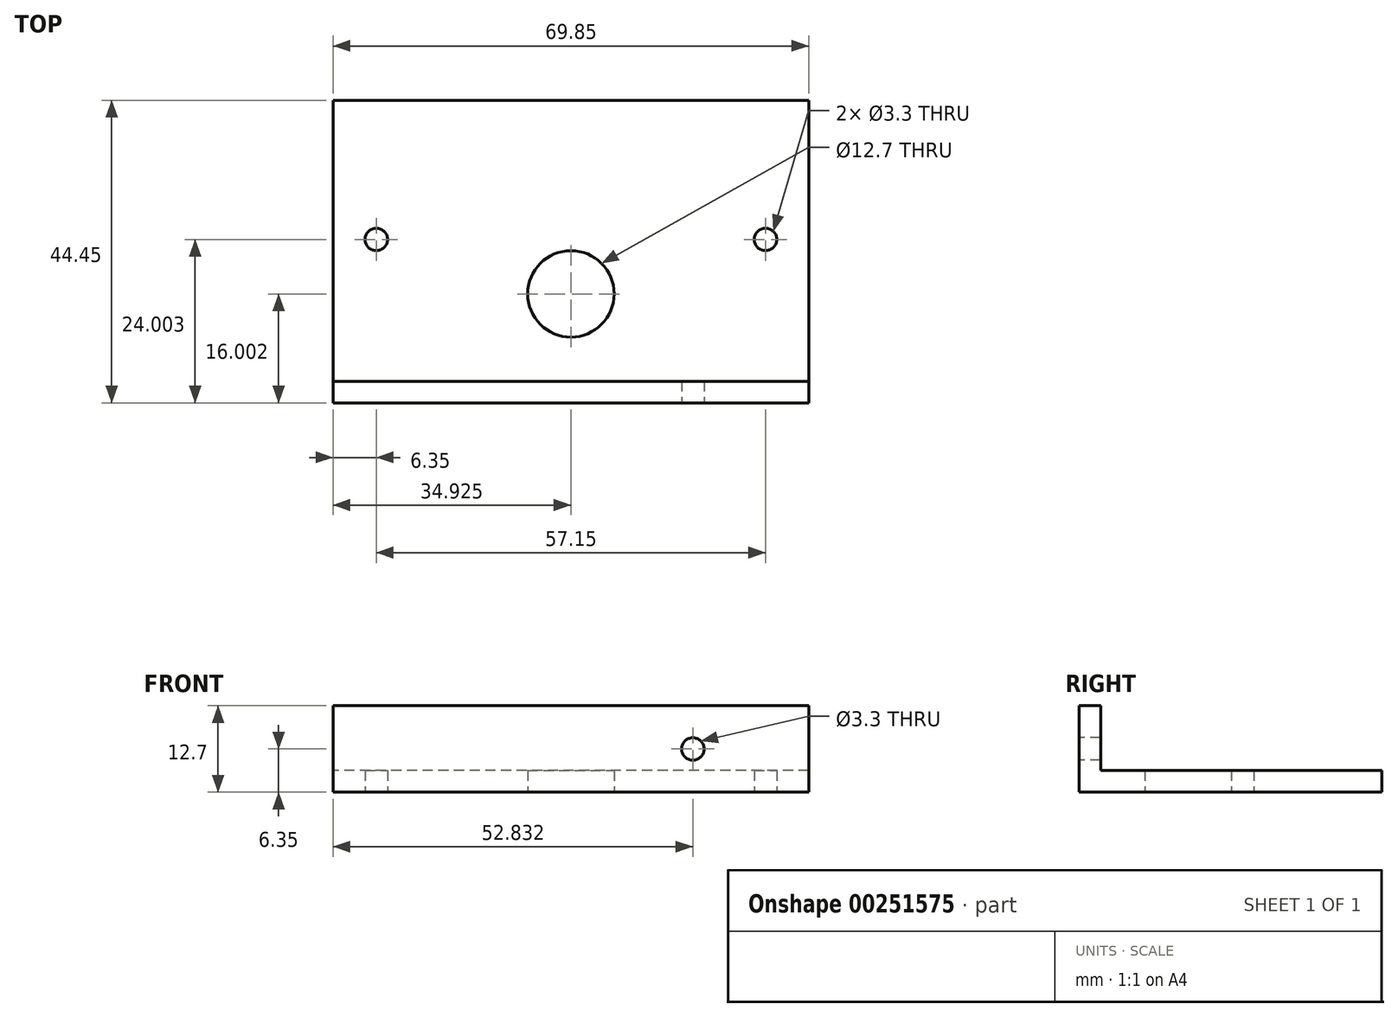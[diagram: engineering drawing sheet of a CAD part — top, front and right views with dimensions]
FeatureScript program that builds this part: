
annotation { "Feature Type Name" : "Feature", "Feature Type Description" : "" }
export const myFeature = defineFeature(function(context is Context, id is Id, definition is map)
    precondition{}
    {
        {
            var Q0;
            Q0=qCreatedBy(makeId("Right.planeOp"),FACE);
            var sketch = newSketch(context, id + "F0", { "sketchPlane" : qUnion([Q0])});
            skLineSegment(sketch, "E0", {"start": v(0, 0) * mm, "end": v(44.45, 0) * mm});
            skLineSegment(sketch, "E1", {"start": v(44.45, 0) * mm, "end": v(44.45, 3.18) * mm});
            skLineSegment(sketch, "E2", {"start": v(44.45, 3.18) * mm, "end": v(3.17, 3.18) * mm});
            skLineSegment(sketch, "E3", {"start": v(3.17, 3.18) * mm, "end": v(3.17, 12.7) * mm});
            skLineSegment(sketch, "E4", {"start": v(3.17, 12.7) * mm, "end": v(0, 12.7) * mm});
            skLineSegment(sketch, "E5", {"start": v(0, 12.7) * mm, "end": v(0, 0) * mm});
            skSolve(sketch);
        }
        {
            var Q0;
            Q0=qSketchRegion(id+"F0",true);
            extrude(context, id + "F1", {"entities" : qUnion([Q0]), "depth" : 69.85 * mm});
        }
        {
            var Q0;
            Q0=makeQuery(id+"F1.opExtrude","SWEPT_FACE",FACE,{"disambiguationData":[OSD([sQuery(id+"F0.wireOp",EDGE,"E0")])]});
            var sketch = newSketch(context, id + "F2", { "sketchPlane" : qUnion([Q0])});
            skPoint(sketch, "E6", {"position": v(6.35, -24) * mm});
            skPoint(sketch, "E7", {"position": v(63.5, -24) * mm});
            skPoint(sketch, "E8", {"position": v(34.93, -16) * mm});
            skSolve(sketch);
        }
        {
            var Q0;
            Q0=sQuery(id+"F2.wireOp",VERTEX,"E6");
            var Q1;
            Q1=sQuery(id+"F2.wireOp",VERTEX,"E7");
            var Q2;
            Q2=makeQuery(id+"F1.opExtrude","SWEPT_BODY",BODY,{"disambiguationData":[OSD([sQuery(id+"F0.wireOp",EDGE,"E0"),sQuery(id+"F0.wireOp",EDGE,"E1"),sQuery(id+"F0.wireOp",EDGE,"E2"),sQuery(id+"F0.wireOp",EDGE,"E3"),sQuery(id+"F0.wireOp",EDGE,"E4"),sQuery(id+"F0.wireOp",EDGE,"E5")])]});
            hole(context, id + "F3", {"style" : HoleStyle.SIMPLE, "endStyle" : HoleEndStyle.THROUGH, "holeDiameter" : 3.3 * mm, "tappedDepth" : 12.7 * mm, "tapClearance" : 3, "startFromSketch" : true, "locations" : qUnion([Q0, Q1]), "scope" : qUnion([Q2])});
        }
        {
            var Q0;
            Q0=makeQuery(id+"F1.opExtrude","SWEPT_FACE",FACE,{"disambiguationData":[OSD([sQuery(id+"F0.wireOp",EDGE,"E5")])]});
            var sketch = newSketch(context, id + "F4", { "sketchPlane" : qUnion([Q0])});
            skPoint(sketch, "E9", {"position": v(52.83, 6.35) * mm});
            skSolve(sketch);
        }
        {
            var Q0;
            Q0=sQuery(id+"F4.wireOp",VERTEX,"E9");
            var Q1;
            Q1=makeQuery(id+"F1.opExtrude","SWEPT_BODY",BODY,{"disambiguationData":[OSD([sQuery(id+"F0.wireOp",EDGE,"E0"),sQuery(id+"F0.wireOp",EDGE,"E1"),sQuery(id+"F0.wireOp",EDGE,"E2"),sQuery(id+"F0.wireOp",EDGE,"E3"),sQuery(id+"F0.wireOp",EDGE,"E4"),sQuery(id+"F0.wireOp",EDGE,"E5")])]});
            hole(context, id + "F5", {"style" : HoleStyle.SIMPLE, "endStyle" : HoleEndStyle.THROUGH, "holeDiameter" : 3.3 * mm, "tappedDepth" : 12.7 * mm, "tapClearance" : 3, "startFromSketch" : true, "locations" : qUnion([Q0]), "scope" : qUnion([Q1])});
        }
        {
            var Q0;
            Q0=sQuery(id+"F2.wireOp",VERTEX,"E8");
            var Q1;
            Q1=makeQuery(id+"F1.opExtrude","SWEPT_BODY",BODY,{"disambiguationData":[OSD([sQuery(id+"F0.wireOp",EDGE,"E0"),sQuery(id+"F0.wireOp",EDGE,"E1"),sQuery(id+"F0.wireOp",EDGE,"E2"),sQuery(id+"F0.wireOp",EDGE,"E3"),sQuery(id+"F0.wireOp",EDGE,"E4"),sQuery(id+"F0.wireOp",EDGE,"E5")])]});
            hole(context, id + "F6", {"style" : HoleStyle.SIMPLE, "endStyle" : HoleEndStyle.THROUGH, "holeDiameter" : 12.7 * mm, "tappedDepth" : 12.7 * mm, "tapClearance" : 3, "startFromSketch" : true, "locations" : qUnion([Q0]), "scope" : qUnion([Q1])});
        }
    });
